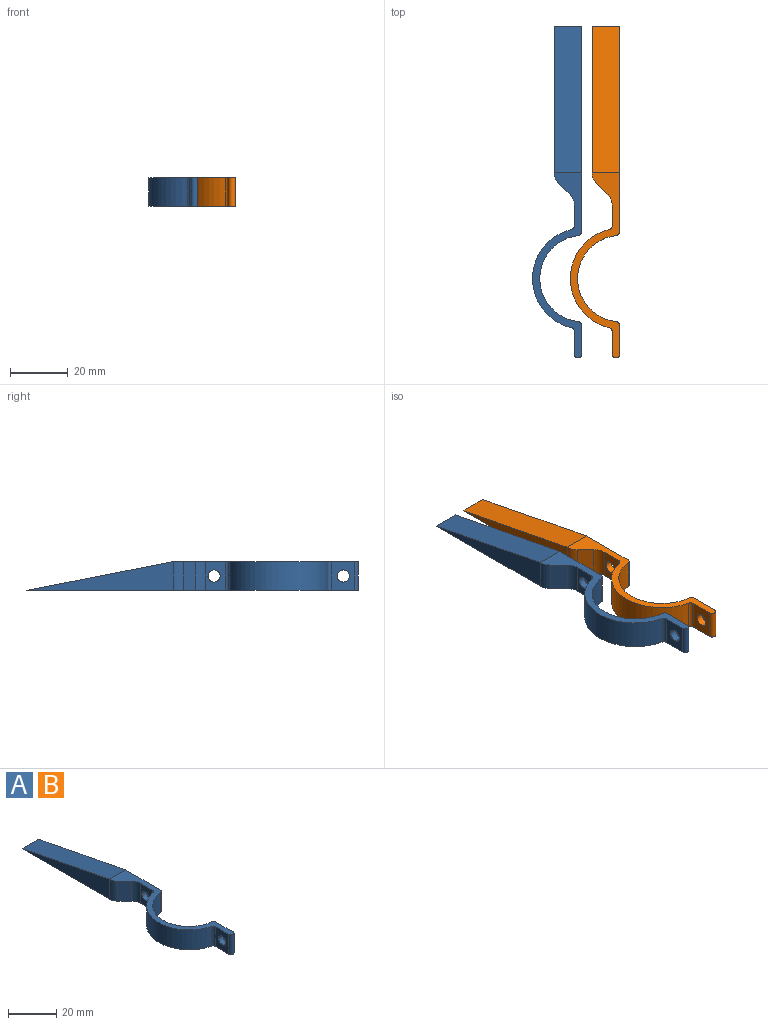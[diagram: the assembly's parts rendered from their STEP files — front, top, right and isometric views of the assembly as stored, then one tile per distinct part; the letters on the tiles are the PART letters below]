
ASSEMBLY  parts=2 mates=1
PART A: 20 faces, bbox 17x115x10 mm
  f0: plane 71.34x10mm, normal (1,0,0), area 444.9mm2, adj f1,f8,f11,f14,f19
  f1: plane 64.06x17mm, normal (0,0,1), area 236.5mm2, adj f0,f2,f3,f5,f6,f7,f9,f12
  f2: plane 10.09x10mm, normal (1,0,0), area 87mm2, adj f1,f8,f10,f16,f18
  f3: cylinder r=15mm len=29.83mm, axis (0,0,-1), area 438.9mm2, adj f1,f8,f18,f19
  f4: plane 50.93x10mm, normal (-1,0,0), area 254.6mm2, adj f8,f12,f14
  f5: plane 10x7.16mm, normal (-1,0,0), area 57.7mm2, adj f1,f8,f11,f13,f17
  f6: cylinder r=17.5mm len=34.09mm, axis (0,0,-1), area 469.7mm2, adj f1,f8,f15,f17
  f7: plane 10x7.98mm, normal (-1,0,0), area 66mm2, adj f1,f8,f10,f15,f16
  f8: plane 114.99x17mm, normal (0,0,-1), area 720.3mm2, adj f0,f2,f3,f4,f5,f6,f7,f9
  f9: plane 10x4.07mm, normal (-0.71,-0.71,0), area 57.6mm2, adj f1,f8,f12,f13
  f10: cylinder r=2.1mm len=4.2mm, axis (-1,0,0), area 33mm2, adj f2,f7
  f11: cylinder r=2.1mm len=4.2mm, axis (-1,0,0), area 33mm2, adj f0,f5
  f12: cylinder r=5mm len=10mm, axis (0,0,-1), area 39.3mm2, adj f1,f4,f8,f9
  f13: cylinder r=5mm len=10mm, axis (0,0,-1), area 39.3mm2, adj f1,f5,f8,f9
  f14: plane 50.93x10mm, normal (0,0.19,0.98), area 493.1mm2, adj f0,f1,f4,f8
  f15: cylinder r=1.25mm len=10mm, axis (0,0,-1), area 16.8mm2, adj f1,f6,f7,f8
  f16: cylinder r=1.25mm len=10mm, axis (0,0,-1), area 39.3mm2, adj f1,f2,f7,f8
  f17: cylinder r=1.25mm len=10mm, axis (0,0,-1), area 16.8mm2, adj f1,f5,f6,f8
  f18: cylinder r=1.25mm len=10mm, axis (0,0,-1), area 18.3mm2, adj f1,f2,f3,f8
  f19: cylinder r=1.25mm len=10mm, axis (0,0,-1), area 18.3mm2, adj f0,f1,f3,f8
PART B: same geometry as A
PLACE A t=(-8.76,-22.49,13.11)mm
PLACE B t=(4.34,-22.49,13.11)mm
MATE planar A.f8 <-> B.f8  axis (0,0,-1) through (-14.61,22.01,13.11)mm
